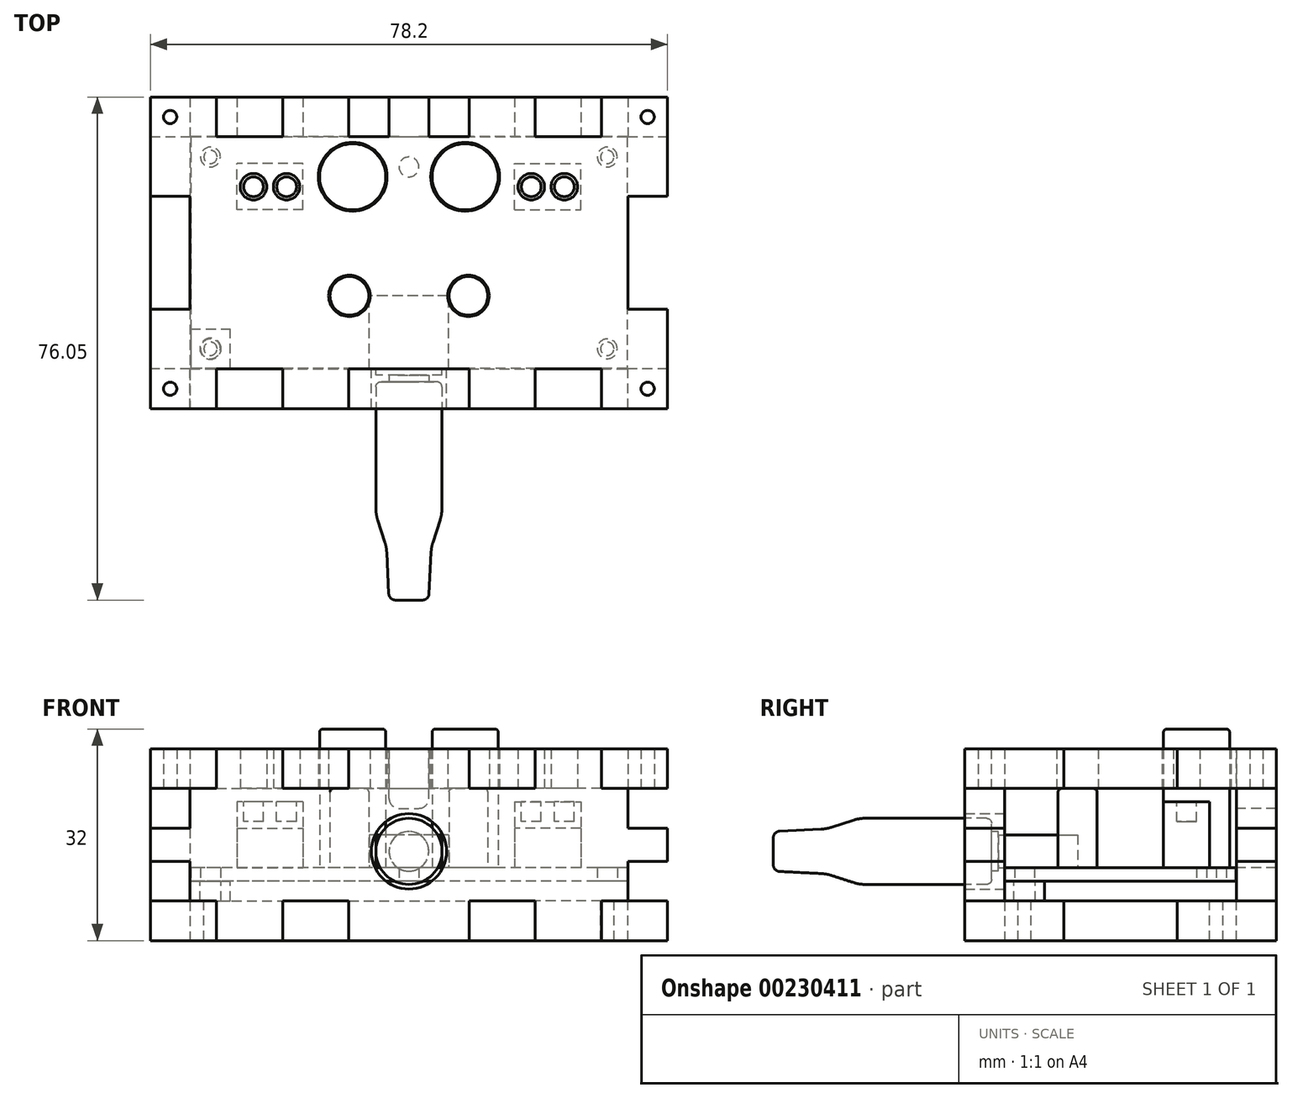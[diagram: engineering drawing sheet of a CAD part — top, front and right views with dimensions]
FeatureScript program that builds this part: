
annotation { "Feature Type Name" : "Feature", "Feature Type Description" : "" }
export const myFeature = defineFeature(function(context is Context, id is Id, definition is map)
    precondition{}
    {
        {
            var Q0;
            Q0=qCreatedBy(makeId("Top.planeOp"),FACE);
            var sketch = newSketch(context, id + "F0", { "sketchPlane" : qUnion([Q0])});
            skLineSegment(sketch, "E0.bottom", {"start": v(33, 17.5) * mm, "end": v(-33, 17.5) * mm});
            skLineSegment(sketch, "E0.top", {"start": v(33, -17.5) * mm, "end": v(-33, -17.5) * mm});
            skLineSegment(sketch, "E0.left", {"start": v(33, 17.5) * mm, "end": v(33, -17.5) * mm});
            skLineSegment(sketch, "E0.right", {"start": v(-33, 17.5) * mm, "end": v(-33, -17.5) * mm});
            skPoint(sketch, "E0.middle", {"position": v(0, 0) * mm});
            skLineSegment(sketch, "E1", {"start": v(0, 0) * mm, "end": v(0, 17.5) * mm, "construction": true});
            skLineSegment(sketch, "E2", {"start": v(0, 0) * mm, "end": v(33, 0) * mm, "construction": true});
            skCircle(sketch, "E3", {"center": v(-30, 14.5) * mm, "radius": 1.5 * mm});
            skCircle(sketch, "E4.MirrorC", {"center": v(30, 14.5) * mm, "radius": 1.5 * mm});
            skCircle(sketch, "E5.MirrorC", {"center": v(30, -14.5) * mm, "radius": 1.5 * mm});
            skCircle(sketch, "E6.MirrorC", {"center": v(-30, -14.5) * mm, "radius": 1.5 * mm});
            skCircle(sketch, "E7", {"center": v(0, 13) * mm, "radius": 1.5 * mm});
            skSolve(sketch);
        }
        {
            var Q0;
            Q0 = qSketchRegion(id + "F0", true);
            extrude(context, id + "F1", {"entities" : qUnion([Q0]), "depth" : 2 * mm});
        }
        {
            var Q0;
            Q0=makeQuery(id+"F1.opExtrude","CAP_FACE",FACE,{"disambiguationData":[OSD([sQuery(id+"F0.wireOp",EDGE,"E0.bottom"),sQuery(id+"F0.wireOp",EDGE,"E0.top"),sQuery(id+"F0.wireOp",EDGE,"E0.left"),sQuery(id+"F0.wireOp",EDGE,"E0.right"),sQuery(id+"F0.wireOp",EDGE,"E3"),sQuery(id+"F0.wireOp",EDGE,"E4.MirrorC"),sQuery(id+"F0.wireOp",EDGE,"E5.MirrorC"),sQuery(id+"F0.wireOp",EDGE,"E6.MirrorC"),sQuery(id+"F0.wireOp",EDGE,"E7")])],"isStart":false});
            var sketch = newSketch(context, id + "F2", { "sketchPlane" : qUnion([Q0])});
            skCircle(sketch, "E8", {"center": v(-8.5, 11.5) * mm, "radius": 5 * mm});
            skCircle(sketch, "E9.MirrorC", {"center": v(8.5, 11.5) * mm, "radius": 5 * mm});
            skSolve(sketch);
        }
        {
            var Q0;
            Q0 = qSketchRegion(id + "F2", true);
            extrude(context, id + "F3", {"entities" : qUnion([Q0]), "operationType" : NewBodyOperationType.ADD, "depth" : 21 * mm});
        }
        {
            var Q0;
            Q0=makeQuery(id+"F1.opExtrude","CAP_FACE",FACE,{"disambiguationData":[OSD([sQuery(id+"F0.wireOp",EDGE,"E0.bottom"),sQuery(id+"F0.wireOp",EDGE,"E0.top"),sQuery(id+"F0.wireOp",EDGE,"E0.left"),sQuery(id+"F0.wireOp",EDGE,"E0.right"),sQuery(id+"F0.wireOp",EDGE,"E3"),sQuery(id+"F0.wireOp",EDGE,"E4.MirrorC"),sQuery(id+"F0.wireOp",EDGE,"E5.MirrorC"),sQuery(id+"F0.wireOp",EDGE,"E6.MirrorC"),sQuery(id+"F0.wireOp",EDGE,"E7")])],"isStart":false});
            var sketch = newSketch(context, id + "F4", { "sketchPlane" : qUnion([Q0])});
            skCircle(sketch, "E10", {"center": v(-9, -6.5) * mm, "radius": 2.93 * mm});
            skCircle(sketch, "E11.MirrorC", {"center": v(9, -6.5) * mm, "radius": 2.93 * mm});
            skSolve(sketch);
        }
        {
            var Q0;
            Q0 = qSketchRegion(id + "F4", true);
            extrude(context, id + "F5", {"entities" : qUnion([Q0]), "operationType" : NewBodyOperationType.ADD, "depth" : 12 * mm});
        }
        {
            var Q0;
            Q0=makeQuery(id+"F1.opExtrude","CAP_FACE",FACE,{"disambiguationData":[OSD([sQuery(id+"F0.wireOp",EDGE,"E0.bottom"),sQuery(id+"F0.wireOp",EDGE,"E0.top"),sQuery(id+"F0.wireOp",EDGE,"E0.left"),sQuery(id+"F0.wireOp",EDGE,"E0.right"),sQuery(id+"F0.wireOp",EDGE,"E3"),sQuery(id+"F0.wireOp",EDGE,"E4.MirrorC"),sQuery(id+"F0.wireOp",EDGE,"E5.MirrorC"),sQuery(id+"F0.wireOp",EDGE,"E6.MirrorC"),sQuery(id+"F0.wireOp",EDGE,"E7")])],"isStart":false});
            var sketch = newSketch(context, id + "F6", { "sketchPlane" : qUnion([Q0])});
            skLineSegment(sketch, "E12.bottom", {"start": v(-16, 6.5) * mm, "end": v(-26, 6.5) * mm});
            skLineSegment(sketch, "E12.top", {"start": v(-16, 13.5) * mm, "end": v(-26, 13.5) * mm});
            skLineSegment(sketch, "E12.left", {"start": v(-16, 6.5) * mm, "end": v(-16, 13.5) * mm});
            skLineSegment(sketch, "E12.right", {"start": v(-26, 6.5) * mm, "end": v(-26, 13.5) * mm});
            skPoint(sketch, "E12.middle", {"position": v(-21, 10) * mm});
            skLineSegment(sketch, "E13.MirrorCS", {"start": v(16, 13.5) * mm, "end": v(26, 13.5) * mm});
            skLineSegment(sketch, "E14.MirrorCS", {"start": v(26, 6.5) * mm, "end": v(26, 13.5) * mm});
            skLineSegment(sketch, "E15.MirrorCS", {"start": v(16, 6.5) * mm, "end": v(26, 6.5) * mm});
            skLineSegment(sketch, "E16.MirrorCS", {"start": v(16, 6.5) * mm, "end": v(16, 13.5) * mm});
            skSolve(sketch);
        }
        {
            var Q0;
            Q0 = qSketchRegion(id + "F6", true);
            extrude(context, id + "F7", {"entities" : qUnion([Q0]), "operationType" : NewBodyOperationType.ADD, "depth" : 10 * mm});
        }
        {
            var Q0;
            Q0=makeQuery(id+"F7.opExtrude","CAP_FACE",FACE,{"disambiguationData":[OSD([sQuery(id+"F6.wireOp",EDGE,"E12.bottom"),sQuery(id+"F6.wireOp",EDGE,"E12.top"),sQuery(id+"F6.wireOp",EDGE,"E12.left"),sQuery(id+"F6.wireOp",EDGE,"E12.right")])],"isStart":false});
            var sketch = newSketch(context, id + "F8", { "sketchPlane" : qUnion([Q0])});
            skLineSegment(sketch, "E17", {"start": v(-23.5, 10) * mm, "end": v(-18.5, 10) * mm, "construction": true});
            skCircle(sketch, "E18", {"center": v(-23.5, 10) * mm, "radius": 1.5 * mm});
            skCircle(sketch, "E19", {"center": v(-18.5, 10) * mm, "radius": 1.5 * mm});
            skCircle(sketch, "E20.MirrorC", {"center": v(23.5, 10) * mm, "radius": 1.5 * mm});
            skCircle(sketch, "E21.MirrorC", {"center": v(18.5, 10) * mm, "radius": 1.5 * mm});
            skSolve(sketch);
        }
        {
            var Q0;
            Q0 = qSketchRegion(id + "F8", true);
            extrude(context, id + "F9", {"entities" : qUnion([Q0]), "operationType" : NewBodyOperationType.REMOVE, "oppositeDirection" : true, "depth" : 3 * mm});
        }
        {
            var Q0;
            Q0=makeQuery(id+"F6.imprint","IMPRINT",FACE,{"disambiguationData":[TD([[makeQuery(id+"F6.imprint","IMPRINT",EDGE,{"derivedFrom":sQuery(id+"F6.wireOp",EDGE,"E12.bottom")}),1.0]])]});
            var sketch = newSketch(context, id + "F10", { "sketchPlane" : qUnion([Q0])});
            skLineSegment(sketch, "E22.bottom", {"start": v(6, -17.5) * mm, "end": v(5, -17.5) * mm});
            skLineSegment(sketch, "E22.top", {"start": v(6, -6.5) * mm, "end": v(-6, -6.5) * mm});
            skLineSegment(sketch, "E22.left", {"start": v(6, -17.5) * mm, "end": v(6, -6.5) * mm});
            skLineSegment(sketch, "E22.right", {"start": v(-6, -17.5) * mm, "end": v(-6, -6.5) * mm});
            skPoint(sketch, "E22.middle", {"position": v(0, -12) * mm});
            skLineSegment(sketch, "E23.bottom", {"start": v(5, -18.5) * mm, "end": v(-5, -18.5) * mm});
            skLineSegment(sketch, "E23.left", {"start": v(5, -18.5) * mm, "end": v(5, -17.5) * mm});
            skLineSegment(sketch, "E23.right", {"start": v(-5, -18.5) * mm, "end": v(-5, -17.5) * mm});
            skPoint(sketch, "E23.middle", {"position": v(0, -17.5) * mm});
            skPoint(sketch, "E24.orphan", {"position": v(-5, -16.5) * mm});
            skLineSegment(sketch, "E25.trimOffspring", {"start": v(-5, -17.5) * mm, "end": v(-6, -17.5) * mm});
            skPoint(sketch, "E26.orphan", {"position": v(5, -16.5) * mm});
            skSolve(sketch);
        }
        {
            var Q0;
            Q0 = qSketchRegion(id + "F10", true);
            extrude(context, id + "F11", {"entities" : qUnion([Q0]), "operationType" : NewBodyOperationType.ADD, "depth" : 5 * mm});
        }
        {
            var Q0;
            Q0=makeQuery(id+"F11.opExtrude","CAP_FACE",FACE,{"disambiguationData":[OSD([sQuery(id+"F10.wireOp",EDGE,"E22.bottom"),sQuery(id+"F10.wireOp",EDGE,"E22.top"),sQuery(id+"F10.wireOp",EDGE,"E22.left"),sQuery(id+"F10.wireOp",EDGE,"E22.right")])],"isStart":false});
            cPlane(context, id + "F12", {"entities" : qUnion([Q0]), "cplaneType" : CPlaneType.OFFSET, "offset" : 2.5 * mm, "oppositeDirection" : true, "width" : 150 * mm, "height" : 150 * mm});
        }
        {
            var Q0;
            Q0=qCreatedBy(id+"F12.planeOp",FACE);
            var sketch = newSketch(context, id + "F13", { "sketchPlane" : qUnion([Q0])});
            skLineSegment(sketch, "E27", {"start": v(0, -18.5) * mm, "end": v(3, -18.5) * mm});
            skLineSegment(sketch, "E28", {"start": v(3, -18.5) * mm, "end": v(3, -19.5) * mm});
            skLineSegment(sketch, "E29", {"start": v(3, -19.5) * mm, "end": v(4.25, -19.5) * mm});
            skLineSegment(sketch, "E30", {"start": v(5, -20.25) * mm, "end": v(5, -38.56) * mm});
            skLineSegment(sketch, "E31", {"start": v(2.05, -52.5) * mm, "end": v(0, -52.5) * mm});
            skLineSegment(sketch, "E32", {"start": v(0, -52.5) * mm, "end": v(0, -18.5) * mm});
            skLineSegment(sketch, "E33", {"start": v(4.71, -40.4) * mm, "end": v(3.63, -43.75) * mm});
            skLineSegment(sketch, "E34", {"start": v(3.35, -45.29) * mm, "end": v(3.05, -51.55) * mm});
            skPoint(sketch, "E35.visualSharp", {"position": v(5, -19.5) * mm});
            skArc(sketch, "E35.filletArc", {"start": v(5, -20.25) * mm, "mid": v(4.78, -19.72) * mm, "end": v(4.25, -19.5) * mm});
            skPoint(sketch, "E36.visualSharp", {"position": v(5, -39.5) * mm});
            skArc(sketch, "E36.filletArc", {"start": v(4.71, -40.4) * mm, "mid": v(4.93, -39.49) * mm, "end": v(5, -38.56) * mm});
            skPoint(sketch, "E37.visualSharp", {"position": v(3.4, -44.5) * mm});
            skArc(sketch, "E37.filletArc", {"start": v(3.63, -43.75) * mm, "mid": v(3.44, -44.5) * mm, "end": v(3.35, -45.29) * mm});
            skPoint(sketch, "E38.visualSharp", {"position": v(3, -52.5) * mm});
            skArc(sketch, "E38.filletArc", {"start": v(2.05, -52.5) * mm, "mid": v(2.74, -52.22) * mm, "end": v(3.05, -51.55) * mm});
            skSolve(sketch);
        }
        {
            var Q0;
            Q0 = qSketchRegion(id + "F13", true);
            var Q1;
            Q1=sQuery(id+"F13.wireOp",EDGE,"E32");
            revolve(context, id + "F14", {"operationType" : NewBodyOperationType.ADD, "entities" : qUnion([Q0]), "axis" : qUnion([Q1]), "revolveType" : RevolveType.FULL});
        }
        {
            var Q0;
            Q0=makeQuery(id+"F3.opExtrude","CAP_EDGE",EDGE,{"disambiguationData":[OSD([sQuery(id+"F2.wireOp",EDGE,"E8")])],"isStart":false});
            var Q1;
            Q1=makeQuery(id+"F3.opExtrude","CAP_EDGE",EDGE,{"disambiguationData":[OSD([sQuery(id+"F2.wireOp",EDGE,"E9.MirrorC")])],"isStart":false});
            var Q2;
            Q2=makeQuery(id+"F5.opExtrude","CAP_EDGE",EDGE,{"disambiguationData":[OSD([sQuery(id+"F4.wireOp",EDGE,"E10")])],"isStart":false});
            var Q3;
            Q3=makeQuery(id+"F5.opExtrude","CAP_EDGE",EDGE,{"disambiguationData":[OSD([sQuery(id+"F4.wireOp",EDGE,"E11.MirrorC")])],"isStart":false});
            fillet(context, id + "F15", {"entities" : qUnion([Q0, Q1, Q2, Q3]), "radius" : .5 * mm, "tangentPropagation" : true, "allowEdgeOverflow" : false});
        }
        {
            assignVariable(context, id + "F16", {"name" : "ply", "anyValue" : 6});
        }
        {
            var Q0;
            Q0=makeQuery(id+"F5.opExtrude","CAP_FACE",FACE,{"disambiguationData":[OSD([sQuery(id+"F4.wireOp",EDGE,"E10")])],"isStart":false});
            var sketch = newSketch(context, id + "F17", { "sketchPlane" : qUnion([Q0])});
            skLineSegment(sketch, "E39.bottom", {"start": v(39.1, 23.55) * mm, "end": v(-39.1, 23.55) * mm, "construction": true});
            skLineSegment(sketch, "E39.top", {"start": v(39.1, -23.55) * mm, "end": v(-39.1, -23.55) * mm, "construction": true});
            skLineSegment(sketch, "E39.left", {"start": v(39.1, 23.55) * mm, "end": v(39.1, -23.55) * mm, "construction": true});
            skLineSegment(sketch, "E39.right", {"start": v(-39.1, 23.55) * mm, "end": v(-39.1, -23.55) * mm, "construction": true});
            skPoint(sketch, "E39.middle", {"position": v(0, 0) * mm});
            skLineSegment(sketch, "E40.bottom", {"start": v(33.1, 17.55) * mm, "end": v(-33.1, 17.55) * mm, "construction": true});
            skLineSegment(sketch, "E40.top", {"start": v(33.1, -17.55) * mm, "end": v(-33.1, -17.55) * mm, "construction": true});
            skLineSegment(sketch, "E40.left", {"start": v(33.1, 17.55) * mm, "end": v(33.1, -17.55) * mm, "construction": true});
            skLineSegment(sketch, "E40.right", {"start": v(-33.1, 17.55) * mm, "end": v(-33.1, -17.55) * mm, "construction": true});
            skCircle(sketch, "E41", {"center": v(-23.5, 10) * mm, "radius": 2 * mm});
            skCircle(sketch, "E42", {"center": v(-18.5, 10) * mm, "radius": 2 * mm});
            skCircle(sketch, "E43.MirrorC", {"center": v(23.5, 10) * mm, "radius": 2 * mm});
            skCircle(sketch, "E44.MirrorC", {"center": v(18.5, 10) * mm, "radius": 2 * mm});
            skCircle(sketch, "E45", {"center": v(-8.5, 11.5) * mm, "radius": 5.2 * mm});
            skCircle(sketch, "E46", {"center": v(8.5, 11.5) * mm, "radius": 5.2 * mm});
            skLineSegment(sketch, "E47", {"start": v(-39.1, 23.55) * mm, "end": v(-29.1, 23.55) * mm});
            skLineSegment(sketch, "E48", {"start": v(-29.1, 23.55) * mm, "end": v(-29.1, 17.55) * mm});
            skLineSegment(sketch, "E49", {"start": v(-29.1, 17.55) * mm, "end": v(-19.1, 17.55) * mm});
            skLineSegment(sketch, "E50", {"start": v(-19.1, 17.55) * mm, "end": v(-19.1, 23.55) * mm});
            skLineSegment(sketch, "E51", {"start": v(-19.1, 23.55) * mm, "end": v(-9.1, 23.55) * mm});
            skLineSegment(sketch, "E52", {"start": v(-9.1, 23.55) * mm, "end": v(-9.1, 17.55) * mm});
            skLineSegment(sketch, "E53", {"start": v(-9.1, 17.55) * mm, "end": v(0, 17.55) * mm});
            skLineSegment(sketch, "E54", {"start": v(0, 0) * mm, "end": v(0, 17.55) * mm, "construction": true});
            skLineSegment(sketch, "E55", {"start": v(0, 0) * mm, "end": v(33.1, 0) * mm, "construction": true});
            skLineSegment(sketch, "E56.MirrorCS", {"start": v(9.1, 23.55) * mm, "end": v(9.1, 17.55) * mm});
            skLineSegment(sketch, "E57.MirrorCS", {"start": v(19.1, 17.55) * mm, "end": v(19.1, 23.55) * mm});
            skLineSegment(sketch, "E58.MirrorCS", {"start": v(9.1, 17.55) * mm, "end": v(0, 17.55) * mm});
            skLineSegment(sketch, "E59.MirrorCS", {"start": v(39.1, 23.55) * mm, "end": v(29.1, 23.55) * mm});
            skLineSegment(sketch, "E60.MirrorCS", {"start": v(19.1, 23.55) * mm, "end": v(9.1, 23.55) * mm});
            skLineSegment(sketch, "E61.MirrorCS", {"start": v(29.1, 17.55) * mm, "end": v(19.1, 17.55) * mm});
            skLineSegment(sketch, "E62.MirrorCS", {"start": v(29.1, 23.55) * mm, "end": v(29.1, 17.55) * mm});
            skLineSegment(sketch, "E63.MirrorCS", {"start": v(-29.1, -17.55) * mm, "end": v(-19.1, -17.55) * mm});
            skLineSegment(sketch, "E64.MirrorCS", {"start": v(-19.1, -23.55) * mm, "end": v(-9.1, -23.55) * mm});
            skLineSegment(sketch, "E65.MirrorCS", {"start": v(29.1, -17.55) * mm, "end": v(19.1, -17.55) * mm});
            skLineSegment(sketch, "E66.MirrorCS", {"start": v(39.1, -23.55) * mm, "end": v(29.1, -23.55) * mm});
            skLineSegment(sketch, "E67.MirrorCS", {"start": v(-39.1, -23.55) * mm, "end": v(-29.1, -23.55) * mm});
            skLineSegment(sketch, "E68.MirrorCS", {"start": v(-9.1, -17.55) * mm, "end": v(0, -17.55) * mm});
            skLineSegment(sketch, "E69.MirrorCS", {"start": v(9.1, -17.55) * mm, "end": v(0, -17.55) * mm});
            skLineSegment(sketch, "E70.MirrorCS", {"start": v(19.1, -23.55) * mm, "end": v(9.1, -23.55) * mm});
            skLineSegment(sketch, "E71.MirrorCS", {"start": v(-29.1, -23.55) * mm, "end": v(-29.1, -17.55) * mm});
            skLineSegment(sketch, "E72.MirrorCS", {"start": v(19.1, -17.55) * mm, "end": v(19.1, -23.55) * mm});
            skLineSegment(sketch, "E73.MirrorCS", {"start": v(29.1, -23.55) * mm, "end": v(29.1, -17.55) * mm});
            skLineSegment(sketch, "E74.MirrorCS", {"start": v(-19.1, -17.55) * mm, "end": v(-19.1, -23.55) * mm});
            skLineSegment(sketch, "E75.MirrorCS", {"start": v(-9.1, -23.55) * mm, "end": v(-9.1, -17.55) * mm});
            skLineSegment(sketch, "E76.MirrorCS", {"start": v(9.1, -23.55) * mm, "end": v(9.1, -17.55) * mm});
            skLineSegment(sketch, "E77", {"start": v(-39.1, 23.55) * mm, "end": v(-39.1, 8.55) * mm});
            skLineSegment(sketch, "E78", {"start": v(-39.1, 8.55) * mm, "end": v(-33.1, 8.55) * mm});
            skLineSegment(sketch, "E79", {"start": v(-33.1, 8.55) * mm, "end": v(-33.1, 0) * mm});
            skLineSegment(sketch, "E80.MirrorCS", {"start": v(-39.1, -23.55) * mm, "end": v(-39.1, -8.55) * mm});
            skLineSegment(sketch, "E81.MirrorCS", {"start": v(-33.1, -8.55) * mm, "end": v(-33.1, 0) * mm});
            skLineSegment(sketch, "E82.MirrorCS", {"start": v(-39.1, -8.55) * mm, "end": v(-33.1, -8.55) * mm});
            skLineSegment(sketch, "E83.MirrorCS", {"start": v(-39.1, -23.55) * mm, "end": v(-39.1, 23.55) * mm, "construction": true});
            skLineSegment(sketch, "E84.MirrorCS", {"start": v(-33.1, -17.55) * mm, "end": v(-33.1, 17.55) * mm, "construction": true});
            skLineSegment(sketch, "E85.MirrorCS", {"start": v(39.1, -23.55) * mm, "end": v(39.1, -8.55) * mm});
            skLineSegment(sketch, "E86.MirrorCS", {"start": v(39.1, 23.55) * mm, "end": v(39.1, 8.55) * mm});
            skLineSegment(sketch, "E87.MirrorCS", {"start": v(39.1, -23.55) * mm, "end": v(39.1, 23.55) * mm, "construction": true});
            skLineSegment(sketch, "E88.MirrorCS", {"start": v(33.1, 8.55) * mm, "end": v(33.1, 0) * mm});
            skLineSegment(sketch, "E89.MirrorCS", {"start": v(39.1, -8.55) * mm, "end": v(33.1, -8.55) * mm});
            skLineSegment(sketch, "E90.MirrorCS", {"start": v(33.1, -8.55) * mm, "end": v(33.1, 0) * mm});
            skLineSegment(sketch, "E91.MirrorCS", {"start": v(39.1, 8.55) * mm, "end": v(33.1, 8.55) * mm});
            skCircle(sketch, "E92", {"center": v(-9, -6.5) * mm, "radius": 3.13 * mm});
            skCircle(sketch, "E93", {"center": v(9, -6.5) * mm, "radius": 3.13 * mm});
            skLineSegment(sketch, "E94.bottom", {"start": v(-3, 23.55) * mm, "end": v(3, 23.55) * mm});
            skLineSegment(sketch, "E94.top", {"start": v(-3, 17.55) * mm, "end": v(3, 17.55) * mm});
            skLineSegment(sketch, "E94.left", {"start": v(-3, 23.55) * mm, "end": v(-3, 17.55) * mm});
            skLineSegment(sketch, "E94.right", {"start": v(3, 23.55) * mm, "end": v(3, 17.55) * mm});
            skLineSegment(sketch, "E95.bottom", {"start": v(-39.1, 23.55) * mm, "end": v(-33.1, 23.55) * mm, "construction": true});
            skLineSegment(sketch, "E95.top", {"start": v(-39.1, 17.55) * mm, "end": v(-33.1, 17.55) * mm, "construction": true});
            skLineSegment(sketch, "E95.left", {"start": v(-39.1, 23.55) * mm, "end": v(-39.1, 17.55) * mm, "construction": true});
            skLineSegment(sketch, "E95.right", {"start": v(-33.1, 23.55) * mm, "end": v(-33.1, 17.55) * mm, "construction": true});
            skCircle(sketch, "E96", {"center": v(-36.1, 20.55) * mm, "radius": 1 * mm});
            skLineSegment(sketch, "E97", {"start": v(-36.1, 20.55) * mm, "end": v(-36.1, 17.55) * mm, "construction": true});
            skPoint(sketch, "E97.endSnap0", {"position": v(-36.1, 17.55) * mm});
            skLineSegment(sketch, "E98", {"start": v(-33.1, 20.55) * mm, "end": v(-36.1, 20.55) * mm, "construction": true});
            skCircle(sketch, "E99.MirrorC", {"center": v(36.1, 20.55) * mm, "radius": 1 * mm});
            skCircle(sketch, "E100.MirrorC", {"center": v(-36.1, -20.55) * mm, "radius": 1 * mm});
            skCircle(sketch, "E101.MirrorC", {"center": v(36.1, -20.55) * mm, "radius": 1 * mm});
            skSolve(sketch);
        }
        {
            var Q0;
            Q0 = qSketchRegion(id + "F17", true);
            extrude(context, id + "F18", {"entities" : qUnion([Q0]), "depth" : (getVariable(context, 'ply')) * mm});
        }
        {
            var Q0;
            Q0=makeQuery(id+"F1.opExtrude","CAP_FACE",FACE,{"disambiguationData":[OSD([sQuery(id+"F0.wireOp",EDGE,"E0.bottom"),sQuery(id+"F0.wireOp",EDGE,"E0.top"),sQuery(id+"F0.wireOp",EDGE,"E0.left"),sQuery(id+"F0.wireOp",EDGE,"E0.right"),sQuery(id+"F0.wireOp",EDGE,"E3"),sQuery(id+"F0.wireOp",EDGE,"E4.MirrorC"),sQuery(id+"F0.wireOp",EDGE,"E5.MirrorC"),sQuery(id+"F0.wireOp",EDGE,"E6.MirrorC"),sQuery(id+"F0.wireOp",EDGE,"E7")])],"isStart":true});
            var sketch = newSketch(context, id + "F19", { "sketchPlane" : qUnion([Q0])});
            skCircle(sketch, "E102", {"center": v(-30, 14.5) * mm, "radius": 1.6 * mm});
            skLineSegment(sketch, "E103.bottom", {"start": v(-33, 17.5) * mm, "end": v(-27, 17.5) * mm});
            skLineSegment(sketch, "E103.top", {"start": v(-33, 11.5) * mm, "end": v(-27, 11.5) * mm});
            skLineSegment(sketch, "E103.left", {"start": v(-33, 17.5) * mm, "end": v(-33, 11.5) * mm});
            skLineSegment(sketch, "E103.right", {"start": v(-27, 17.5) * mm, "end": v(-27, 11.5) * mm});
            skSolve(sketch);
        }
        {
            var Q0;
            Q0 = qSketchRegion(id + "F19", true);
            extrude(context, id + "F20", {"entities" : qUnion([Q0]), "depth" : 3 * mm});
        }
        {
            var Q0;
            Q0=makeQuery(id+"F20.opExtrude","CAP_FACE",FACE,{"disambiguationData":[OSD([sQuery(id+"F19.wireOp",EDGE,"E102"),sQuery(id+"F19.wireOp",EDGE,"E103.bottom"),sQuery(id+"F19.wireOp",EDGE,"E103.top"),sQuery(id+"F19.wireOp",EDGE,"E103.left"),sQuery(id+"F19.wireOp",EDGE,"E103.right")])],"isStart":false});
            var sketch = newSketch(context, id + "F21", { "sketchPlane" : qUnion([Q0])});
            skLineSegment(sketch, "E104.bottom", {"start": v(39.1, 23.55) * mm, "end": v(-39.1, 23.55) * mm, "construction": true});
            skLineSegment(sketch, "E104.top", {"start": v(39.1, -23.55) * mm, "end": v(-39.1, -23.55) * mm, "construction": true});
            skLineSegment(sketch, "E104.left", {"start": v(39.1, 23.55) * mm, "end": v(39.1, -23.55) * mm, "construction": true});
            skLineSegment(sketch, "E104.right", {"start": v(-39.1, 23.55) * mm, "end": v(-39.1, -23.55) * mm, "construction": true});
            skPoint(sketch, "E104.middle", {"position": v(0, 0) * mm});
            skLineSegment(sketch, "E105.bottom", {"start": v(33.1, 17.55) * mm, "end": v(-33.1, 17.55) * mm, "construction": true});
            skLineSegment(sketch, "E105.top", {"start": v(33.1, -17.55) * mm, "end": v(-33.1, -17.55) * mm, "construction": true});
            skLineSegment(sketch, "E105.left", {"start": v(33.1, 17.55) * mm, "end": v(33.1, -17.55) * mm, "construction": true});
            skLineSegment(sketch, "E105.right", {"start": v(-33.1, 17.55) * mm, "end": v(-33.1, -17.55) * mm, "construction": true});
            skLineSegment(sketch, "E106", {"start": v(-39.1, 23.55) * mm, "end": v(-29.1, 23.55) * mm});
            skLineSegment(sketch, "E107", {"start": v(-29.1, 23.55) * mm, "end": v(-29.1, 17.55) * mm});
            skLineSegment(sketch, "E108", {"start": v(-29.1, 17.55) * mm, "end": v(-19.1, 17.55) * mm});
            skLineSegment(sketch, "E109", {"start": v(-19.1, 17.55) * mm, "end": v(-19.1, 23.55) * mm});
            skLineSegment(sketch, "E110", {"start": v(-19.1, 23.55) * mm, "end": v(-9.1, 23.55) * mm});
            skLineSegment(sketch, "E111", {"start": v(-9.1, 23.55) * mm, "end": v(-9.1, 17.55) * mm});
            skLineSegment(sketch, "E112", {"start": v(-9.1, 17.55) * mm, "end": v(0, 17.55) * mm});
            skLineSegment(sketch, "E113", {"start": v(0, 0) * mm, "end": v(0, 17.55) * mm, "construction": true});
            skLineSegment(sketch, "E114", {"start": v(0, 0) * mm, "end": v(33.1, 0) * mm, "construction": true});
            skLineSegment(sketch, "E115.MirrorCS", {"start": v(9.1, 23.55) * mm, "end": v(9.1, 17.55) * mm});
            skLineSegment(sketch, "E116.MirrorCS", {"start": v(19.1, 17.55) * mm, "end": v(19.1, 23.55) * mm});
            skLineSegment(sketch, "E117.MirrorCS", {"start": v(9.1, 17.55) * mm, "end": v(0, 17.55) * mm});
            skLineSegment(sketch, "E118.MirrorCS", {"start": v(39.1, 23.55) * mm, "end": v(29.1, 23.55) * mm});
            skLineSegment(sketch, "E119.MirrorCS", {"start": v(19.1, 23.55) * mm, "end": v(9.1, 23.55) * mm});
            skLineSegment(sketch, "E120.MirrorCS", {"start": v(29.1, 17.55) * mm, "end": v(19.1, 17.55) * mm});
            skLineSegment(sketch, "E121.MirrorCS", {"start": v(29.1, 23.55) * mm, "end": v(29.1, 17.55) * mm});
            skLineSegment(sketch, "E122.MirrorCS", {"start": v(-29.1, -17.55) * mm, "end": v(-19.1, -17.55) * mm});
            skLineSegment(sketch, "E123.MirrorCS", {"start": v(-19.1, -23.55) * mm, "end": v(-9.1, -23.55) * mm});
            skLineSegment(sketch, "E124.MirrorCS", {"start": v(29.1, -17.55) * mm, "end": v(19.1, -17.55) * mm});
            skLineSegment(sketch, "E125.MirrorCS", {"start": v(39.1, -23.55) * mm, "end": v(29.1, -23.55) * mm});
            skLineSegment(sketch, "E126.MirrorCS", {"start": v(-39.1, -23.55) * mm, "end": v(-29.1, -23.55) * mm});
            skLineSegment(sketch, "E127.MirrorCS", {"start": v(-9.1, -17.55) * mm, "end": v(0, -17.55) * mm});
            skLineSegment(sketch, "E128.MirrorCS", {"start": v(9.1, -17.55) * mm, "end": v(0, -17.55) * mm});
            skLineSegment(sketch, "E129.MirrorCS", {"start": v(19.1, -23.55) * mm, "end": v(9.1, -23.55) * mm});
            skLineSegment(sketch, "E130.MirrorCS", {"start": v(-29.1, -23.55) * mm, "end": v(-29.1, -17.55) * mm});
            skLineSegment(sketch, "E131.MirrorCS", {"start": v(19.1, -17.55) * mm, "end": v(19.1, -23.55) * mm});
            skLineSegment(sketch, "E132.MirrorCS", {"start": v(29.1, -23.55) * mm, "end": v(29.1, -17.55) * mm});
            skLineSegment(sketch, "E133.MirrorCS", {"start": v(-19.1, -17.55) * mm, "end": v(-19.1, -23.55) * mm});
            skLineSegment(sketch, "E134.MirrorCS", {"start": v(-9.1, -23.55) * mm, "end": v(-9.1, -17.55) * mm});
            skLineSegment(sketch, "E135.MirrorCS", {"start": v(9.1, -23.55) * mm, "end": v(9.1, -17.55) * mm});
            skLineSegment(sketch, "E136", {"start": v(-39.1, 23.55) * mm, "end": v(-39.1, 8.55) * mm});
            skLineSegment(sketch, "E137", {"start": v(-39.1, 8.55) * mm, "end": v(-33.1, 8.55) * mm});
            skLineSegment(sketch, "E138", {"start": v(-33.1, 8.55) * mm, "end": v(-33.1, 0) * mm});
            skLineSegment(sketch, "E139.MirrorCS", {"start": v(-39.1, -23.55) * mm, "end": v(-39.1, -8.55) * mm});
            skLineSegment(sketch, "E140.MirrorCS", {"start": v(-33.1, -8.55) * mm, "end": v(-33.1, 0) * mm});
            skLineSegment(sketch, "E141.MirrorCS", {"start": v(-39.1, -8.55) * mm, "end": v(-33.1, -8.55) * mm});
            skLineSegment(sketch, "E142.MirrorCS", {"start": v(-39.1, -23.55) * mm, "end": v(-39.1, 23.55) * mm, "construction": true});
            skLineSegment(sketch, "E143.MirrorCS", {"start": v(-33.1, -17.55) * mm, "end": v(-33.1, 17.55) * mm, "construction": true});
            skLineSegment(sketch, "E144.MirrorCS", {"start": v(39.1, -23.55) * mm, "end": v(39.1, -8.55) * mm});
            skLineSegment(sketch, "E145.MirrorCS", {"start": v(39.1, 23.55) * mm, "end": v(39.1, 8.55) * mm});
            skLineSegment(sketch, "E146.MirrorCS", {"start": v(39.1, -23.55) * mm, "end": v(39.1, 23.55) * mm, "construction": true});
            skLineSegment(sketch, "E147.MirrorCS", {"start": v(33.1, 8.55) * mm, "end": v(33.1, 0) * mm});
            skLineSegment(sketch, "E148.MirrorCS", {"start": v(39.1, -8.55) * mm, "end": v(33.1, -8.55) * mm});
            skLineSegment(sketch, "E149.MirrorCS", {"start": v(33.1, -8.55) * mm, "end": v(33.1, 0) * mm});
            skLineSegment(sketch, "E150.MirrorCS", {"start": v(39.1, 8.55) * mm, "end": v(33.1, 8.55) * mm});
            skCircle(sketch, "E151", {"center": v(-30, 14.5) * mm, "radius": 1 * mm});
            skCircle(sketch, "E152.MirrorC", {"center": v(30, 14.5) * mm, "radius": 1 * mm});
            skCircle(sketch, "E153.MirrorC", {"center": v(30, -14.5) * mm, "radius": 1 * mm});
            skCircle(sketch, "E154.MirrorC", {"center": v(-30, -14.5) * mm, "radius": 1 * mm});
            skSolve(sketch);
        }
        {
            var Q0;
            Q0 = qSketchRegion(id + "F21", true);
            extrude(context, id + "F22", {"entities" : qUnion([Q0]), "depth" : (getVariable(context, 'ply')) * mm});
        }
        {
            var Q0;
            Q0=makeQuery(id+"F18.opExtrude","SWEPT_FACE",FACE,{"disambiguationData":[OSD([sQuery(id+"F17.wireOp",EDGE,"E79"),sQuery(id+"F17.wireOp",EDGE,"E81.MirrorCS")])]});
            var sketch = newSketch(context, id + "F23", { "sketchPlane" : qUnion([Q0])});
            skLineSegment(sketch, "E155", {"start": v(-23.55, 14) * mm, "end": v(-8.55, 14) * mm});
            skLineSegment(sketch, "E156", {"start": v(-8.55, 14) * mm, "end": v(-8.55, 20) * mm});
            skLineSegment(sketch, "E157", {"start": v(-8.55, 20) * mm, "end": v(8.55, 20) * mm});
            skLineSegment(sketch, "E158", {"start": v(8.55, 20) * mm, "end": v(8.55, 14) * mm});
            skLineSegment(sketch, "E159", {"start": v(8.55, 14) * mm, "end": v(23.55, 14) * mm});
            skLineSegment(sketch, "E160", {"start": v(-23.55, -3) * mm, "end": v(-8.55, -3) * mm});
            skLineSegment(sketch, "E161", {"start": v(-8.55, -3) * mm, "end": v(-8.55, -9) * mm});
            skLineSegment(sketch, "E162", {"start": v(-8.55, -9) * mm, "end": v(8.55, -9) * mm});
            skLineSegment(sketch, "E163", {"start": v(8.55, -9) * mm, "end": v(8.55, -3) * mm});
            skLineSegment(sketch, "E164", {"start": v(8.55, -3) * mm, "end": v(23.55, -3) * mm});
            skLineSegment(sketch, "E165", {"start": v(-23.55, 14) * mm, "end": v(-23.55, 8) * mm});
            skLineSegment(sketch, "E166", {"start": v(-23.55, 8) * mm, "end": v(-17.55, 8) * mm});
            skLineSegment(sketch, "E167", {"start": v(-17.55, 8) * mm, "end": v(-17.55, 3) * mm});
            skLineSegment(sketch, "E168", {"start": v(-17.55, 3) * mm, "end": v(-23.55, 3) * mm});
            skLineSegment(sketch, "E169", {"start": v(-23.55, 3) * mm, "end": v(-23.55, -3) * mm});
            skLineSegment(sketch, "E170", {"start": v(23.55, 14) * mm, "end": v(23.55, 8) * mm});
            skLineSegment(sketch, "E171", {"start": v(23.55, 8) * mm, "end": v(17.55, 8) * mm});
            skLineSegment(sketch, "E172", {"start": v(17.55, 8) * mm, "end": v(17.55, 3) * mm});
            skLineSegment(sketch, "E173", {"start": v(17.55, 3) * mm, "end": v(23.55, 3) * mm});
            skLineSegment(sketch, "E174", {"start": v(23.55, 3) * mm, "end": v(23.55, -3) * mm});
            skSolve(sketch);
        }
        {
            var Q0;
            Q0 = qSketchRegion(id + "F23", true);
            extrude(context, id + "F24", {"entities" : qUnion([Q0]), "depth" : (getVariable(context, 'ply')) * mm});
        }
        {
            var Q0;
            Q0=makeQuery(id+"F22.opExtrude","SWEPT_FACE",FACE,{"disambiguationData":[OSD([sQuery(id+"F21.wireOp",EDGE,"E127.MirrorCS"),sQuery(id+"F21.wireOp",EDGE,"E128.MirrorCS")])]});
            var sketch = newSketch(context, id + "F25", { "sketchPlane" : qUnion([Q0])});
            skLineSegment(sketch, "E175", {"start": v(-33.1, 14) * mm, "end": v(-29.1, 14) * mm});
            skLineSegment(sketch, "E176", {"start": v(-29.1, 14) * mm, "end": v(-29.1, 20) * mm});
            skLineSegment(sketch, "E177", {"start": v(-29.1, 20) * mm, "end": v(-19.1, 20) * mm});
            skLineSegment(sketch, "E178", {"start": v(-19.1, 20) * mm, "end": v(-19.1, 14) * mm});
            skLineSegment(sketch, "E179", {"start": v(-19.1, 14) * mm, "end": v(-9.1, 14) * mm});
            skLineSegment(sketch, "E180", {"start": v(-9.1, 14) * mm, "end": v(-9.1, 20) * mm});
            skLineSegment(sketch, "E181", {"start": v(-9.1, 20) * mm, "end": v(-3, 20) * mm});
            skLineSegment(sketch, "E182", {"start": v(9.1, 20) * mm, "end": v(9.1, 14) * mm});
            skLineSegment(sketch, "E183", {"start": v(9.1, 14) * mm, "end": v(19.1, 14) * mm});
            skLineSegment(sketch, "E184", {"start": v(19.1, 14) * mm, "end": v(19.1, 20) * mm});
            skLineSegment(sketch, "E185", {"start": v(19.1, 20) * mm, "end": v(29.1, 20) * mm});
            skLineSegment(sketch, "E186", {"start": v(29.1, 20) * mm, "end": v(29.1, 14) * mm});
            skLineSegment(sketch, "E187", {"start": v(29.1, 14) * mm, "end": v(33.1, 14) * mm});
            skLineSegment(sketch, "E188", {"start": v(0, 14) * mm, "end": v(0, -3) * mm, "construction": true});
            skLineSegment(sketch, "E189", {"start": v(0, 5.5) * mm, "end": v(-3.6, 5.5) * mm, "construction": true});
            skLineSegment(sketch, "E190.MirrorCS", {"start": v(19.1, -3) * mm, "end": v(19.1, -9) * mm});
            skLineSegment(sketch, "E191.MirrorCS", {"start": v(19.1, -9) * mm, "end": v(29.1, -9) * mm});
            skLineSegment(sketch, "E192.MirrorCS", {"start": v(9.1, -3) * mm, "end": v(19.1, -3) * mm});
            skLineSegment(sketch, "E193.MirrorCS", {"start": v(29.1, -9) * mm, "end": v(29.1, -3) * mm});
            skLineSegment(sketch, "E194.MirrorCS", {"start": v(9.1, -9) * mm, "end": v(9.1, -3) * mm});
            skLineSegment(sketch, "E195.MirrorCS", {"start": v(29.1, -3) * mm, "end": v(33.1, -3) * mm});
            skLineSegment(sketch, "E196.MirrorCS", {"start": v(-9.1, -9) * mm, "end": v(9.1, -9) * mm});
            skLineSegment(sketch, "E197.MirrorCS", {"start": v(-9.1, -3) * mm, "end": v(-9.1, -9) * mm});
            skLineSegment(sketch, "E198.MirrorCS", {"start": v(-19.1, -3) * mm, "end": v(-9.1, -3) * mm});
            skLineSegment(sketch, "E199.MirrorCS", {"start": v(-19.1, -9) * mm, "end": v(-19.1, -3) * mm});
            skLineSegment(sketch, "E200.MirrorCS", {"start": v(-33.1, -3) * mm, "end": v(-29.1, -3) * mm});
            skLineSegment(sketch, "E201.MirrorCS", {"start": v(-29.1, -3) * mm, "end": v(-29.1, -9) * mm});
            skLineSegment(sketch, "E202.MirrorCS", {"start": v(-29.1, -9) * mm, "end": v(-19.1, -9) * mm});
            skLineSegment(sketch, "E203", {"start": v(33.1, 14) * mm, "end": v(33.1, 8) * mm});
            skLineSegment(sketch, "E204", {"start": v(33.1, 8) * mm, "end": v(39.1, 8) * mm});
            skLineSegment(sketch, "E205", {"start": v(39.1, 8) * mm, "end": v(39.1, 3) * mm});
            skLineSegment(sketch, "E206", {"start": v(39.1, 3) * mm, "end": v(33.1, 3) * mm});
            skLineSegment(sketch, "E207", {"start": v(33.1, 3) * mm, "end": v(33.1, -3) * mm});
            skLineSegment(sketch, "E208.MirrorCS", {"start": v(-39.1, 8) * mm, "end": v(-39.1, 3) * mm});
            skLineSegment(sketch, "E209.MirrorCS", {"start": v(-39.1, 3) * mm, "end": v(-33.1, 3) * mm});
            skLineSegment(sketch, "E210.MirrorCS", {"start": v(-33.1, 8) * mm, "end": v(-39.1, 8) * mm});
            skLineSegment(sketch, "E211.MirrorCS", {"start": v(-33.1, 14) * mm, "end": v(-33.1, 8) * mm});
            skLineSegment(sketch, "E212.MirrorCS", {"start": v(-33.1, 3) * mm, "end": v(-33.1, -3) * mm});
            skLineSegment(sketch, "E213.bottom", {"start": v(-26, 8) * mm, "end": v(-16, 8) * mm});
            skLineSegment(sketch, "E213.top", {"start": v(-26, 2) * mm, "end": v(-16, 2) * mm});
            skLineSegment(sketch, "E213.left", {"start": v(-26, 8) * mm, "end": v(-26, 2) * mm});
            skLineSegment(sketch, "E213.right", {"start": v(-16, 8) * mm, "end": v(-16, 2) * mm});
            skLineSegment(sketch, "E214.MirrorCS", {"start": v(26, 2) * mm, "end": v(16, 2) * mm});
            skLineSegment(sketch, "E215.MirrorCS", {"start": v(26, 8) * mm, "end": v(26, 2) * mm});
            skLineSegment(sketch, "E216.MirrorCS", {"start": v(16, 8) * mm, "end": v(16, 2) * mm});
            skLineSegment(sketch, "E217.MirrorCS", {"start": v(26, 8) * mm, "end": v(16, 8) * mm});
            skLineSegment(sketch, "E218.bottom", {"start": v(1.5, 11) * mm, "end": v(-1.5, 11) * mm});
            skLineSegment(sketch, "E218.left", {"start": v(3, 12.5) * mm, "end": v(3, 12.5) * mm});
            skLineSegment(sketch, "E218.right", {"start": v(-3, 12.5) * mm, "end": v(-3, 12.5) * mm});
            skPoint(sketch, "E218.middle", {"position": v(0, 12.5) * mm});
            skPoint(sketch, "E219.visualSharp", {"position": v(-3, 14) * mm});
            skPoint(sketch, "E220.visualSharp", {"position": v(-3, 11) * mm});
            skArc(sketch, "E220.filletArc", {"start": v(-3, 12.5) * mm, "mid": v(-2.56, 11.44) * mm, "end": v(-1.5, 11) * mm});
            skPoint(sketch, "E221.visualSharp", {"position": v(3, 14) * mm});
            skPoint(sketch, "E222.visualSharp", {"position": v(3, 11) * mm});
            skArc(sketch, "E222.filletArc", {"start": v(1.5, 11) * mm, "mid": v(2.56, 11.44) * mm, "end": v(3, 12.5) * mm});
            skLineSegment(sketch, "E223", {"start": v(-3, 12.5) * mm, "end": v(-3, 14) * mm, "construction": true});
            skLineSegment(sketch, "E224", {"start": v(-3, 14) * mm, "end": v(3, 14) * mm, "construction": true});
            skLineSegment(sketch, "E225", {"start": v(3, 14) * mm, "end": v(3, 12.5) * mm, "construction": true});
            skLineSegment(sketch, "E226", {"start": v(-3, 12.5) * mm, "end": v(-3, 20) * mm});
            skLineSegment(sketch, "E227", {"start": v(3, 12.5) * mm, "end": v(3, 20) * mm});
            skLineSegment(sketch, "E228.trimOffspring", {"start": v(3, 20) * mm, "end": v(9.1, 20) * mm});
            skLineSegment(sketch, "E229", {"start": v(-3, 20) * mm, "end": v(3, 20) * mm, "construction": true});
            skSolve(sketch);
        }
        {
            var Q0;
            Q0=makeQuery(id+"F18.opExtrude","SWEPT_FACE",FACE,{"disambiguationData":[OSD([sQuery(id+"F17.wireOp",EDGE,"E63.MirrorCS")])]});
            var sketch = newSketch(context, id + "F26", { "sketchPlane" : qUnion([Q0])});
            skLineSegment(sketch, "E230", {"start": v(-33.1, 14) * mm, "end": v(-29.1, 14) * mm});
            skLineSegment(sketch, "E231", {"start": v(-29.1, 14) * mm, "end": v(-29.1, 20) * mm});
            skLineSegment(sketch, "E232", {"start": v(-29.1, 20) * mm, "end": v(-19.1, 20) * mm});
            skLineSegment(sketch, "E233", {"start": v(-19.1, 20) * mm, "end": v(-19.1, 14) * mm});
            skLineSegment(sketch, "E234", {"start": v(-19.1, 14) * mm, "end": v(-9.1, 14) * mm});
            skLineSegment(sketch, "E235", {"start": v(-9.1, 14) * mm, "end": v(-9.1, 20) * mm});
            skLineSegment(sketch, "E236", {"start": v(-9.1, 20) * mm, "end": v(9.1, 20) * mm});
            skLineSegment(sketch, "E237", {"start": v(9.1, 20) * mm, "end": v(9.1, 14) * mm});
            skLineSegment(sketch, "E238", {"start": v(9.1, 14) * mm, "end": v(19.1, 14) * mm});
            skLineSegment(sketch, "E239", {"start": v(19.1, 14) * mm, "end": v(19.1, 20) * mm});
            skLineSegment(sketch, "E240", {"start": v(19.1, 20) * mm, "end": v(29.1, 20) * mm});
            skLineSegment(sketch, "E241", {"start": v(29.1, 20) * mm, "end": v(29.1, 14) * mm});
            skLineSegment(sketch, "E242", {"start": v(29.1, 14) * mm, "end": v(33.1, 14) * mm});
            skLineSegment(sketch, "E243", {"start": v(0, 9.53) * mm, "end": v(0, 1.47) * mm, "construction": true});
            skLineSegment(sketch, "E244", {"start": v(0, 5.5) * mm, "end": v(-39.84, 5.5) * mm, "construction": true});
            skLineSegment(sketch, "E245.MirrorCS", {"start": v(19.1, -3) * mm, "end": v(19.1, -9) * mm});
            skLineSegment(sketch, "E246.MirrorCS", {"start": v(19.1, -9) * mm, "end": v(29.1, -9) * mm});
            skLineSegment(sketch, "E247.MirrorCS", {"start": v(9.1, -3) * mm, "end": v(19.1, -3) * mm});
            skLineSegment(sketch, "E248.MirrorCS", {"start": v(29.1, -9) * mm, "end": v(29.1, -3) * mm});
            skLineSegment(sketch, "E249.MirrorCS", {"start": v(9.1, -9) * mm, "end": v(9.1, -3) * mm});
            skLineSegment(sketch, "E250.MirrorCS", {"start": v(29.1, -3) * mm, "end": v(33.1, -3) * mm});
            skLineSegment(sketch, "E251.MirrorCS", {"start": v(-9.1, -9) * mm, "end": v(9.1, -9) * mm});
            skLineSegment(sketch, "E252.MirrorCS", {"start": v(-9.1, -3) * mm, "end": v(-9.1, -9) * mm});
            skLineSegment(sketch, "E253.MirrorCS", {"start": v(-19.1, -3) * mm, "end": v(-9.1, -3) * mm});
            skLineSegment(sketch, "E254.MirrorCS", {"start": v(-19.1, -9) * mm, "end": v(-19.1, -3) * mm});
            skLineSegment(sketch, "E255.MirrorCS", {"start": v(-33.1, -3) * mm, "end": v(-29.1, -3) * mm});
            skLineSegment(sketch, "E256.MirrorCS", {"start": v(-29.1, -3) * mm, "end": v(-29.1, -9) * mm});
            skLineSegment(sketch, "E257.MirrorCS", {"start": v(-29.1, -9) * mm, "end": v(-19.1, -9) * mm});
            skLineSegment(sketch, "E258", {"start": v(33.1, 14) * mm, "end": v(33.1, 8) * mm});
            skLineSegment(sketch, "E259", {"start": v(33.1, 8) * mm, "end": v(39.1, 8) * mm});
            skLineSegment(sketch, "E260", {"start": v(39.1, 8) * mm, "end": v(39.1, 3) * mm});
            skLineSegment(sketch, "E261", {"start": v(39.1, 3) * mm, "end": v(33.1, 3) * mm});
            skLineSegment(sketch, "E262", {"start": v(33.1, 3) * mm, "end": v(33.1, -3) * mm});
            skLineSegment(sketch, "E263.MirrorCS", {"start": v(-39.1, 8) * mm, "end": v(-39.1, 3) * mm});
            skLineSegment(sketch, "E264.MirrorCS", {"start": v(-39.1, 3) * mm, "end": v(-33.1, 3) * mm});
            skLineSegment(sketch, "E265.MirrorCS", {"start": v(-33.1, 8) * mm, "end": v(-39.1, 8) * mm});
            skLineSegment(sketch, "E266.MirrorCS", {"start": v(-33.1, 14) * mm, "end": v(-33.1, 8) * mm});
            skLineSegment(sketch, "E267.MirrorCS", {"start": v(-33.1, 3) * mm, "end": v(-33.1, -3) * mm});
            skCircle(sketch, "E268", {"center": v(0, 4.5) * mm, "radius": 5.7 * mm});
            skSolve(sketch);
        }
        {
            var Q0;
            Q0 = qSketchRegion(id + "F26", true);
            extrude(context, id + "F27", {"entities" : qUnion([Q0]), "depth" : (getVariable(context, 'ply')) * mm});
        }
        {
            var Q0;
            Q0 = qSketchRegion(id + "F25", true);
            extrude(context, id + "F28", {"entities" : qUnion([Q0]), "depth" : (getVariable(context, 'ply')) * mm});
        }
    });
